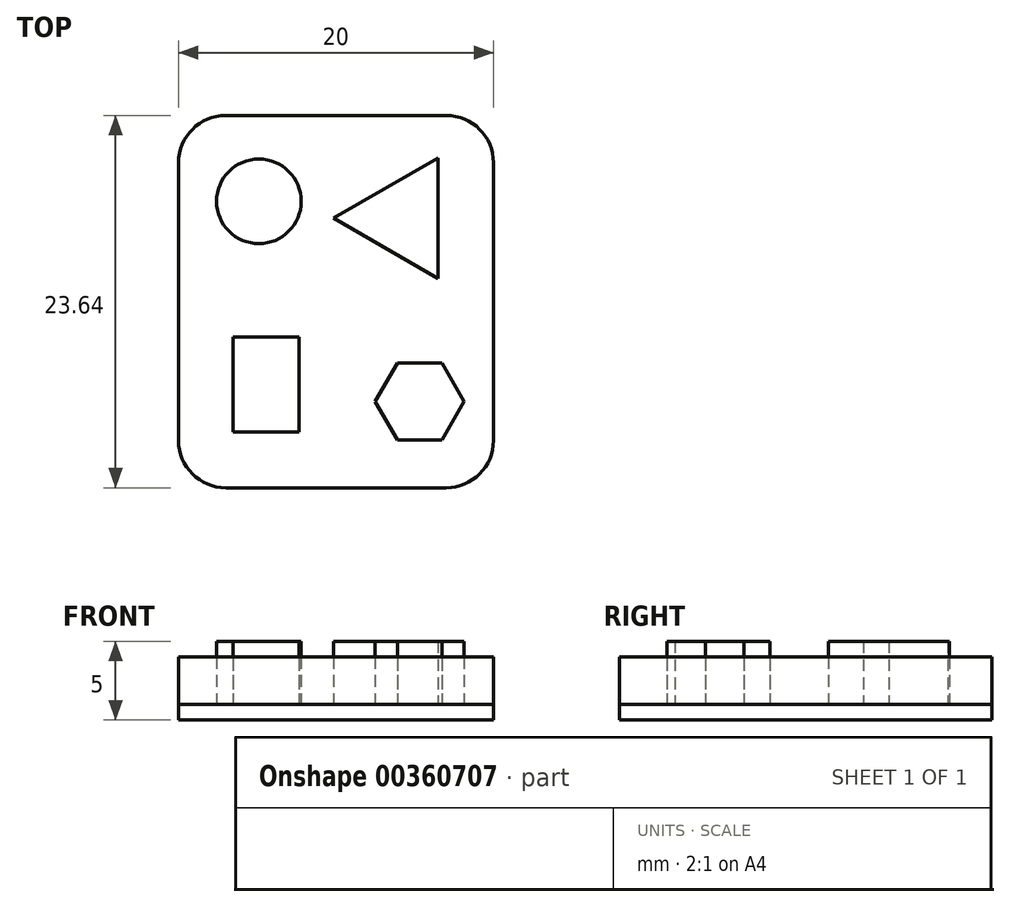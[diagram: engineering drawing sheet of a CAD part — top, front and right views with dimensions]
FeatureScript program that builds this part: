
annotation { "Feature Type Name" : "Feature", "Feature Type Description" : "" }
export const myFeature = defineFeature(function(context is Context, id is Id, definition is map)
    precondition{}
    {
        {
            var Q0;
            Q0=qCreatedBy(makeId("Top.planeOp"),FACE);
            var sketch = newSketch(context, id + "F0", { "sketchPlane" : qUnion([Q0])});
            skLineSegment(sketch, "E0.bottom", {"start": v(7, -11.82) * mm, "end": v(-7, -11.82) * mm});
            skLineSegment(sketch, "E0.top", {"start": v(7, 11.82) * mm, "end": v(-7, 11.82) * mm});
            skLineSegment(sketch, "E0.left", {"start": v(10, -8.82) * mm, "end": v(10, 8.82) * mm});
            skLineSegment(sketch, "E0.right", {"start": v(-10, -8.82) * mm, "end": v(-10, 8.82) * mm});
            skPoint(sketch, "E0.middle", {"position": v(0, 0) * mm});
            skPoint(sketch, "E1.visualSharp", {"position": v(10, 11.82) * mm});
            skArc(sketch, "E1.filletArc", {"start": v(10, 8.82) * mm, "mid": v(9.12, 10.94) * mm, "end": v(7, 11.82) * mm});
            skPoint(sketch, "E2.visualSharp", {"position": v(-10, 11.82) * mm});
            skArc(sketch, "E2.filletArc", {"start": v(-7, 11.82) * mm, "mid": v(-9.12, 10.94) * mm, "end": v(-10, 8.82) * mm});
            skPoint(sketch, "E3.visualSharp", {"position": v(-10, -11.82) * mm});
            skArc(sketch, "E3.filletArc", {"start": v(-10, -8.82) * mm, "mid": v(-9.12, -10.94) * mm, "end": v(-7, -11.82) * mm});
            skPoint(sketch, "E4.visualSharp", {"position": v(10, -11.82) * mm});
            skArc(sketch, "E4.filletArc", {"start": v(7, -11.82) * mm, "mid": v(9.12, -10.94) * mm, "end": v(10, -8.82) * mm});
            skSolve(sketch);
        }
        {
            var Q0;
            Q0=makeQuery(id+"F0.imprint","IMPRINT",FACE,{"disambiguationData":[TD([[makeQuery(id+"F0.imprint","IMPRINT",EDGE,{"derivedFrom":sQuery(id+"F0.wireOp",EDGE,"E0.bottom")}),-1.0]])]});
            extrude(context, id + "F1", {"entities" : qUnion([Q0]), "offsetDistance" : 25 * mm, "depth" : 1 * mm});
        }
        {
            var Q0;
            Q0=makeQuery(id+"F1.opExtrude","CAP_FACE",FACE,{"disambiguationData":[OSD([sQuery(id+"F0.wireOp",EDGE,"E0.bottom"),sQuery(id+"F0.wireOp",EDGE,"E0.top"),sQuery(id+"F0.wireOp",EDGE,"E0.left"),sQuery(id+"F0.wireOp",EDGE,"E0.right")])],"isStart":false});
            var sketch = newSketch(context, id + "F2", { "sketchPlane" : qUnion([Q0])});
            skCircle(sketch, "E5", {"center": v(-4.9, 6.37) * mm, "radius": 2.69 * mm});
            skCircle(sketch, "E6.cCircle", {"center": v(5.31, -6.35) * mm, "radius": 2.45 * mm, "construction": true});
            skLineSegment(sketch, "E6.0", {"start": v(3.9, -3.9) * mm, "end": v(6.73, -3.9) * mm});
            skLineSegment(sketch, "E6.1", {"start": v(6.73, -3.9) * mm, "end": v(8.14, -6.35) * mm});
            skLineSegment(sketch, "E6.2", {"start": v(8.14, -6.35) * mm, "end": v(6.73, -8.8) * mm});
            skLineSegment(sketch, "E6.3", {"start": v(6.73, -8.8) * mm, "end": v(3.9, -8.8) * mm});
            skLineSegment(sketch, "E6.4", {"start": v(3.9, -8.8) * mm, "end": v(2.48, -6.35) * mm});
            skLineSegment(sketch, "E6.5", {"start": v(2.48, -6.35) * mm, "end": v(3.9, -3.9) * mm});
            skPoint(sketch, "E6.0.midPoint", {"position": v(5.31, -3.9) * mm});
            skLineSegment(sketch, "E7.bottom", {"start": v(-2.36, -2.26) * mm, "end": v(-6.55, -2.26) * mm});
            skLineSegment(sketch, "E7.top", {"start": v(-2.36, -8.28) * mm, "end": v(-6.55, -8.28) * mm});
            skLineSegment(sketch, "E7.left", {"start": v(-2.36, -2.26) * mm, "end": v(-2.36, -8.28) * mm});
            skLineSegment(sketch, "E7.right", {"start": v(-6.55, -2.26) * mm, "end": v(-6.55, -8.28) * mm});
            skPoint(sketch, "E7.middle", {"position": v(-4.45, -5.27) * mm});
            skCircle(sketch, "E8.cCircle", {"center": v(4.25, 5.3) * mm, "radius": 2.21 * mm, "construction": true});
            skLineSegment(sketch, "E8.0", {"start": v(6.46, 9.12) * mm, "end": v(6.46, 1.47) * mm});
            skLineSegment(sketch, "E8.1", {"start": v(6.46, 1.47) * mm, "end": v(-0.17, 5.3) * mm});
            skLineSegment(sketch, "E8.2", {"start": v(-0.17, 5.3) * mm, "end": v(6.46, 9.12) * mm});
            skPoint(sketch, "E8.0.midPoint", {"position": v(6.46, 5.3) * mm});
            skSolve(sketch);
        }
        {
            var Q0;
            Q0=makeQuery(id+"F2.imprint","IMPRINT",FACE,{"disambiguationData":[TD([[makeQuery(id+"F2.imprint","IMPRINT",EDGE,{"derivedFrom":sQuery(id+"F2.wireOp",EDGE,"E5")}),1.0]])]});
            var Q1;
            Q1=makeQuery(id+"F2.imprint","IMPRINT",FACE,{"disambiguationData":[TD([[makeQuery(id+"F2.imprint","IMPRINT",EDGE,{"derivedFrom":sQuery(id+"F2.wireOp",EDGE,"E7.bottom")}),1.0]])]});
            var Q2;
            Q2=makeQuery(id+"F2.imprint","IMPRINT",FACE,{"disambiguationData":[TD([[makeQuery(id+"F2.imprint","IMPRINT",EDGE,{"derivedFrom":sQuery(id+"F2.wireOp",EDGE,"E6.0")}),-1.0]])]});
            var Q3;
            Q3=makeQuery(id+"F2.imprint","IMPRINT",FACE,{"disambiguationData":[TD([[makeQuery(id+"F2.imprint","IMPRINT",EDGE,{"derivedFrom":sQuery(id+"F2.wireOp",EDGE,"E8.0")}),-1.0]])]});
            extrude(context, id + "F3", {"entities" : qUnion([Q0, Q1, Q2, Q3]), "operationType" : NewBodyOperationType.ADD, "offsetDistance" : 25 * mm, "depth" : 4 * mm});
        }
        {
            var Q0;
            Q0=makeQuery(id+"F0.imprint","IMPRINT",FACE,{"disambiguationData":[TD([[makeQuery(id+"F0.imprint","IMPRINT",EDGE,{"derivedFrom":sQuery(id+"F0.wireOp",EDGE,"E0.bottom")}),-1.0]])]});
            extrude(context, id + "F4", {"entities" : qUnion([Q0]), "offsetDistance" : 25 * mm, "depth" : 4 * mm});
        }
    });
